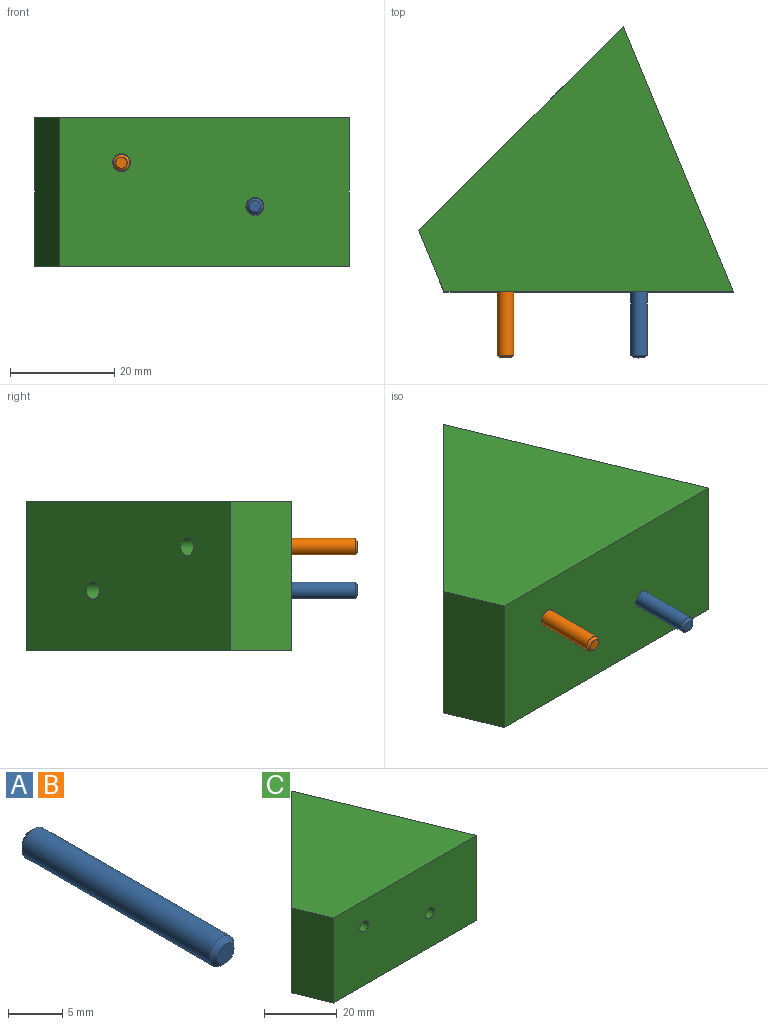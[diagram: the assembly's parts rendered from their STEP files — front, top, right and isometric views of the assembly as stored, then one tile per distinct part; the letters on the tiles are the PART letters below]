
ASSEMBLY  parts=3 mates=2
PART A: 5 faces, bbox 3.2x25.4x3.2 mm
  f0: cylinder r=1.59mm len=24.38mm, axis (0,-1,0), area 243.2mm2, adj f3,f4
  f1: plane 2.16x2.16mm, normal (0,1,0), area 3.7mm2, adj f3
  f2: plane 2.16x2.16mm, normal (0,-1,0), area 3.7mm2, adj f4
  f3: cone r=1.59mm half-angle=45deg, axis (0,-1,0), area 6mm2, adj f0,f1
  f4: cone r=1.08mm half-angle=45deg, axis (0,1,0), area 6mm2, adj f0,f2
PART B: same geometry as A
PART C: 14 faces, bbox 60.5x51.1x28.6 mm
  f0: plane 55.62x28.58mm, normal (0,-1,0), area 1570.7mm2, adj f1,f3,f4,f5,f7,f9
  f1: plane 51.09x28.58mm, normal (0.92,0.38,0), area 1580.2mm2, adj f0,f2,f4,f5
  f2: plane 39.33x39.33mm, normal (-0.71,0.71,0), area 1570.7mm2, adj f1,f3,f4,f5,f11,f13
  f3: plane 28.58x11.76mm, normal (-0.92,-0.38,0), area 363.7mm2, adj f0,f2,f4,f5
  f4: plane 60.49x51.09mm, normal (0,0,1), area 1747.9mm2, adj f0,f1,f2,f3
  f5: plane 60.49x51.09mm, normal (0,0,-1), area 1747.9mm2, adj f0,f1,f2,f3
  f6: cone r=0mm half-angle=59deg, axis (0,-1,0), area 10.9mm2, adj f7
  f7: cylinder r=1.73mm len=6.73mm, axis (0,-1,0), area 73mm2, adj f0,f6
  f8: cone r=0mm half-angle=59deg, axis (0,-1,0), area 10.9mm2, adj f9
  f9: cylinder r=1.73mm len=6.73mm, axis (0,-1,0), area 73mm2, adj f0,f8
  f10: cone r=0mm half-angle=59deg, axis (-0.71,0.71,0), area 10.9mm2, adj f11
  f11: cylinder r=1.73mm len=7.2mm, axis (-0.71,0.71,0), area 73mm2, adj f2,f10
  f12: cone r=0mm half-angle=59deg, axis (-0.71,0.71,0), area 10.9mm2, adj f13
  f13: cylinder r=1.73mm len=7.2mm, axis (-0.71,0.71,0), area 73mm2, adj f2,f12
PLACE A t=(54.1,-12.7,46.74)mm
PLACE B t=(28.45,-12.7,55.12)mm
PLACE C at identity
MATE revolute B.f0 <-> C.f8  axis (0,-1,0) through (28.45,0,55.12)mm
MATE revolute A.f0 <-> C.f6  axis (0,-1,0) through (54.1,0,46.74)mm
